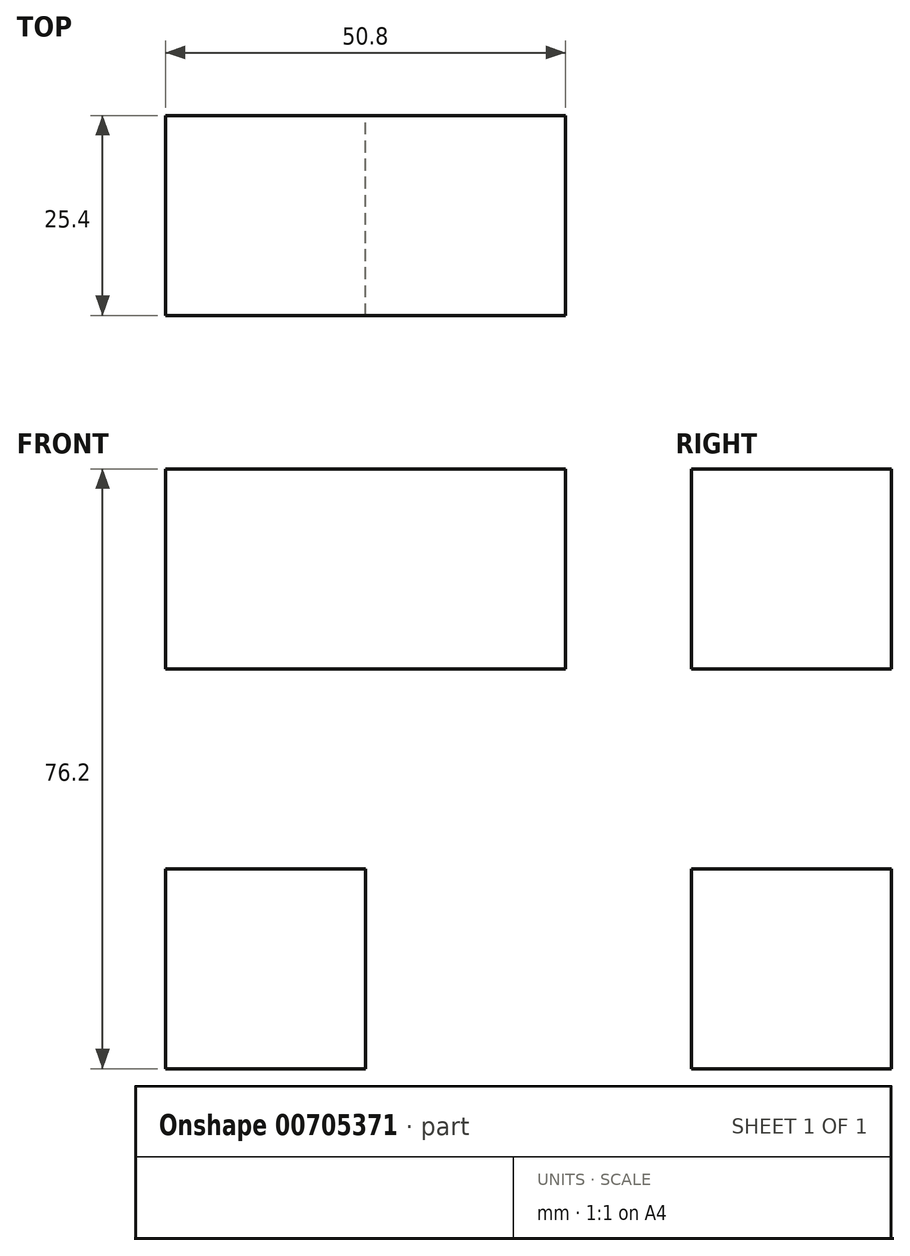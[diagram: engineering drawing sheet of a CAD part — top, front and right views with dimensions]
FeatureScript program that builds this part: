
annotation { "Feature Type Name" : "Feature", "Feature Type Description" : "" }
export const myFeature = defineFeature(function(context is Context, id is Id, definition is map)
    precondition{}
    {
        {
            var Q0;
            Q0=qCreatedBy(makeId("Front.planeOp"),FACE);
            var sketch = newSketch(context, id + "F0", { "sketchPlane" : qUnion([Q0])});
            skLineSegment(sketch, "E0.bottom", {"start": v(0, 0) * mm, "end": v(-25.4, 0) * mm});
            skLineSegment(sketch, "E0.top", {"start": v(0, 25.4) * mm, "end": v(-25.4, 25.4) * mm});
            skLineSegment(sketch, "E0.left", {"start": v(0, 0) * mm, "end": v(0, 25.4) * mm});
            skLineSegment(sketch, "E0.right", {"start": v(-25.4, 0) * mm, "end": v(-25.4, 25.4) * mm});
            skLineSegment(sketch, "E1.bottom", {"start": v(-25.4, 25.4) * mm, "end": v(0, 25.4) * mm});
            skLineSegment(sketch, "E1.top", {"start": v(-25.4, 50.8) * mm, "end": v(0, 50.8) * mm});
            skLineSegment(sketch, "E1.left", {"start": v(-25.4, 25.4) * mm, "end": v(-25.4, 50.8) * mm});
            skLineSegment(sketch, "E1.right", {"start": v(0, 25.4) * mm, "end": v(0, 50.8) * mm});
            skLineSegment(sketch, "E2.top", {"start": v(-25.4, 76.2) * mm, "end": v(0, 76.2) * mm});
            skLineSegment(sketch, "E2.left", {"start": v(-25.4, 50.8) * mm, "end": v(-25.4, 76.2) * mm});
            skLineSegment(sketch, "E2.right", {"start": v(0, 50.8) * mm, "end": v(0, 76.2) * mm});
            skLineSegment(sketch, "E3.bottom", {"start": v(0, 76.2) * mm, "end": v(25.4, 76.2) * mm});
            skLineSegment(sketch, "E3.top", {"start": v(0, 50.8) * mm, "end": v(25.4, 50.8) * mm});
            skLineSegment(sketch, "E3.left", {"start": v(0, 76.2) * mm, "end": v(0, 50.8) * mm});
            skLineSegment(sketch, "E3.right", {"start": v(25.4, 76.2) * mm, "end": v(25.4, 50.8) * mm});
            skLineSegment(sketch, "E4.bottom", {"start": v(25.4, 50.8) * mm, "end": v(0, 50.8) * mm});
            skLineSegment(sketch, "E4.top", {"start": v(25.4, 25.4) * mm, "end": v(0, 25.4) * mm});
            skLineSegment(sketch, "E4.left", {"start": v(25.4, 50.8) * mm, "end": v(25.4, 25.4) * mm});
            skLineSegment(sketch, "E4.right", {"start": v(0, 50.8) * mm, "end": v(0, 25.4) * mm});
            skLineSegment(sketch, "E5.bottom", {"start": v(0, 25.4) * mm, "end": v(25.4, 25.4) * mm});
            skLineSegment(sketch, "E5.top", {"start": v(0, 0) * mm, "end": v(25.4, 0) * mm});
            skLineSegment(sketch, "E5.left", {"start": v(0, 25.4) * mm, "end": v(0, 0) * mm});
            skLineSegment(sketch, "E5.right", {"start": v(25.4, 25.4) * mm, "end": v(25.4, 0) * mm});
            skSolve(sketch);
        }
        {
            var Q0;
            Q0=makeQuery(id+"F0.imprint","IMPRINT",FACE,{"disambiguationData":[TD([[makeQuery(id+"F0.imprint","IMPRINT",EDGE,{"derivedFrom":sQuery(id+"F0.wireOp",EDGE,"E0.bottom")}),-1.0]])]});
            var Q1;
            Q1=makeQuery(id+"F0.imprint","IMPRINT",FACE,{"disambiguationData":[TD([[makeQuery(id+"F0.imprint","IMPRINT",EDGE,{"derivedFrom":sQuery(id+"F0.wireOp",EDGE,"E5.bottom")}),-1.0]])]});
            var Q2;
            Q2=makeQuery(id+"F0.imprint","IMPRINT",FACE,{"disambiguationData":[TD([[makeQuery(id+"F0.imprint","IMPRINT",EDGE,{"derivedFrom":sQuery(id+"F0.wireOp",EDGE,"E1.bottom")}),1.0]])]});
            var Q3;
            Q3=makeQuery(id+"F0.imprint","IMPRINT",FACE,{"disambiguationData":[TD([[makeQuery(id+"F0.imprint","IMPRINT",EDGE,{"derivedFrom":sQuery(id+"F0.wireOp",EDGE,"E4.bottom")}),1.0]])]});
            var Q4;
            Q4=makeQuery(id+"F0.imprint","IMPRINT",FACE,{"disambiguationData":[TD([[makeQuery(id+"F0.imprint","IMPRINT",EDGE,{"derivedFrom":sQuery(id+"F0.wireOp",EDGE,"E1.top")}),1.0]])]});
            var Q5;
            Q5=makeQuery(id+"F0.imprint","IMPRINT",FACE,{"disambiguationData":[TD([[makeQuery(id+"F0.imprint","IMPRINT",EDGE,{"derivedFrom":sQuery(id+"F0.wireOp",EDGE,"E3.bottom")}),-1.0]])]});
            extrude(context, id + "F1", {"entities" : qUnion([Q0, Q1, Q2, Q3, Q4, Q5]), "depth" : 25.4 * mm, "offsetDistance" : 25.4 * mm});
        }
    });
